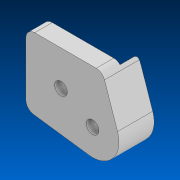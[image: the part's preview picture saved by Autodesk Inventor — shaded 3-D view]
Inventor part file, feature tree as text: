
AUTODESK INVENTOR PART (.ipt)
format: ipt  version: 2022 (Build 260153000, 153)  size: 152,576 bytes
history: native  units: in
note: dims shown in document units (in); Inventor stores cm internally (conversion verified against a paired STEP export)
features: extrude x3, fillet x2
ambient origin geometry x8: Origin, YZ Plane, XZ Plane, XY Plane, X Axis, Y Axis, Z Axis, Center Point
bodies: Solid1 (feature_tree)
feature tree (5):
  extrude  "Extrusion1"  Depth=1.0in
  extrude  "Extrusion2"  Depth=1.0in
  extrude  "Extrusion3"  Depth=0.75in
  fillet  "Fillet2"  Radius=0.335in
  fillet  "Fillet1"  Radius=0.18in
